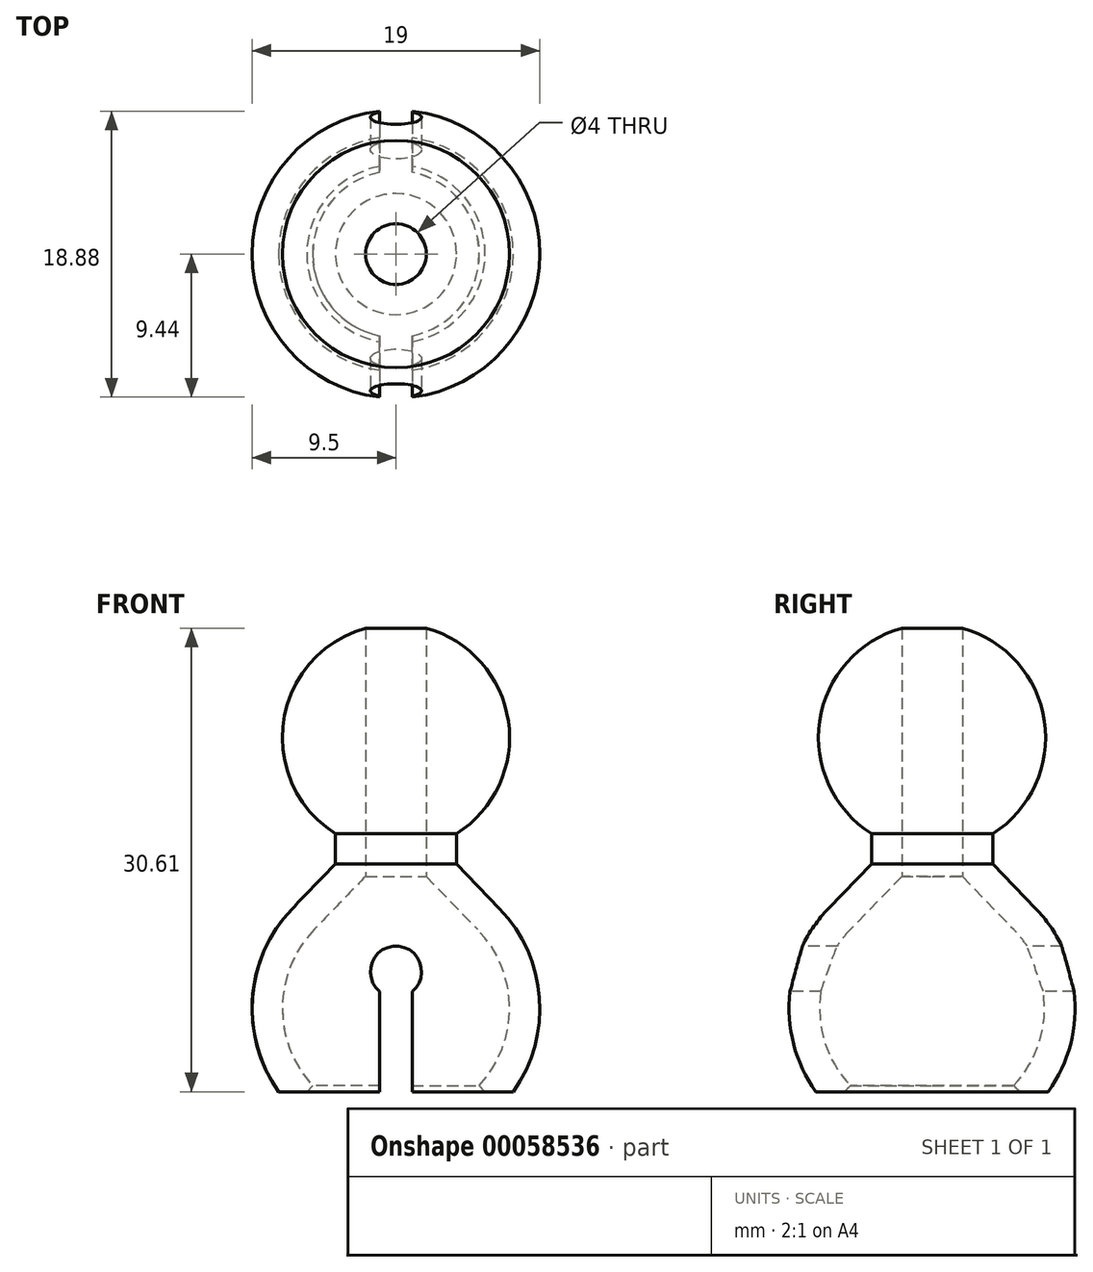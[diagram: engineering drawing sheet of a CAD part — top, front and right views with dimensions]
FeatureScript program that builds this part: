
annotation { "Feature Type Name" : "Feature", "Feature Type Description" : "" }
export const myFeature = defineFeature(function(context is Context, id is Id, definition is map)
    precondition{}
    {
        {
            var Q0;
            Q0=qCreatedBy(makeId("Front.planeOp"),FACE);
            var sketch = newSketch(context, id + "F0", { "sketchPlane" : qUnion([Q0])});
            skCircle(sketch, "E0", {"center": v(0, 0) * mm, "radius": 7.5 * mm});
            skCircle(sketch, "E1", {"center": v(0, 17.88) * mm, "radius": 7.5 * mm});
            skLineSegment(sketch, "E2", {"start": v(-5.4, -5.2) * mm, "end": v(-2, -8.73) * mm});
            skLineSegment(sketch, "E3", {"start": v(0, -8.73) * mm, "end": v(-5.24, -8.73) * mm, "construction": true});
            skLineSegment(sketch, "E4.MirrorCS", {"start": v(-5.4, 5.2) * mm, "end": v(-2, 8.73) * mm});
            skPoint(sketch, "E5", {"position": v(-7.5, 0) * mm});
            skLineSegment(sketch, "E6", {"start": v(-5.5, -5.1) * mm, "end": v(0, -5.1) * mm});
            skArc(sketch, "E7", {"start": v(-6.83, 6.6) * mm, "mid": v(-9.47, 0.71) * mm, "end": v(-7.75, -5.5) * mm});
            skLineSegment(sketch, "E8", {"start": v(-6.83, 6.6) * mm, "end": v(-4, 9.53) * mm});
            skLineSegment(sketch, "E9", {"start": v(-5.5, -5.1) * mm, "end": v(-5.89, -5.5) * mm});
            skLineSegment(sketch, "E10", {"start": v(-5.89, -5.5) * mm, "end": v(-7.75, -5.5) * mm});
            skLineSegment(sketch, "E11", {"start": v(0, -7.5) * mm, "end": v(0, 25.38) * mm});
            skLineSegment(sketch, "E12", {"start": v(-2, 25.1) * mm, "end": v(-2, -7.23) * mm});
            skLineSegment(sketch, "E13", {"start": v(-4, 11.53) * mm, "end": v(-4, 9.53) * mm});
            skSolve(sketch);
        }
        {
            var Q0;
            {var subQ0=sQuery(id+"F0.wireOp",EDGE,"E12");var subQ1=sQuery(id+"F0.wireOp",EDGE,"E1");var subQ2=makeQuery(id+"F0.imprint","INTERSECT",VERTEX,{"disambiguationData":[OD(0.0)],"derivedFrom":[subQ1,subQ0]});Q0=makeQuery(id+"F0.imprint","IMPRINT",FACE,{"disambiguationData":[TD([[makeQuery(id+"F0.imprint","IMPRINT",EDGE,{"disambiguationData":[TD([[subQ2,-1.0]])],"derivedFrom":subQ1}),1.0]])]});}
            var Q1;
            {var subQ0=sQuery(id+"F0.wireOp",EDGE,"E4.MirrorCS");Q1=makeQuery(id+"F0.imprint","IMPRINT",FACE,{"disambiguationData":[TD([[makeQuery(id+"F0.imprint","IMPRINT",EDGE,{"derivedFrom":subQ0}),1.0]])]});}
            var Q2;
            Q2=sQuery(id+"F0.wireOp",EDGE,"E11");
            revolve(context, id + "F1", {"entities" : qUnion([Q0, Q1]), "axis" : qUnion([Q2]), "revolveType" : RevolveType.FULL});
        }
        {
            var Q0;
            Q0=qCreatedBy(makeId("Front.planeOp"),FACE);
            var sketch = newSketch(context, id + "F2", { "sketchPlane" : qUnion([Q0])});
            skCircle(sketch, "E14", {"center": v(0, 2.42) * mm, "radius": 1.7 * mm});
            skLineSegment(sketch, "E15", {"start": v(-1.07, 1.1) * mm, "end": v(-1.07, -9.65) * mm});
            skLineSegment(sketch, "E16.MirrorCS", {"start": v(1.07, 1.1) * mm, "end": v(1.07, -9.65) * mm});
            skLineSegment(sketch, "E17", {"start": v(-1.07, -9.65) * mm, "end": v(1.07, -9.65) * mm});
            skSolve(sketch);
        }
        {
            var Q0;
            {var subQ0=sQuery(id+"F2.wireOp",EDGE,"E14");var subQ1=makeQuery(id+"F2.imprint","INTERSECT",VERTEX,{"derivedFrom":[subQ0,sQuery(id+"F2.wireOp",EDGE,"E15")]});Q0=makeQuery(id+"F2.imprint","IMPRINT",FACE,{"disambiguationData":[TD([[makeQuery(id+"F2.imprint","IMPRINT",EDGE,{"disambiguationData":[TD([[subQ1,-1.0]])],"derivedFrom":subQ0}),1.0]])]});}
            var Q1;
            {var subQ0=sQuery(id+"F2.wireOp",EDGE,"E15");Q1=makeQuery(id+"F2.imprint","IMPRINT",FACE,{"disambiguationData":[TD([[makeQuery(id+"F2.imprint","IMPRINT",EDGE,{"derivedFrom":subQ0}),1.0]])]});}
            extrude(context, id + "F3", {"entities" : qUnion([Q0, Q1]), "operationType" : NewBodyOperationType.REMOVE, "endBound" : BoundingType.SYMMETRIC, "oppositeDirection" : true, "depth" : 25 * mm});
        }
    });
